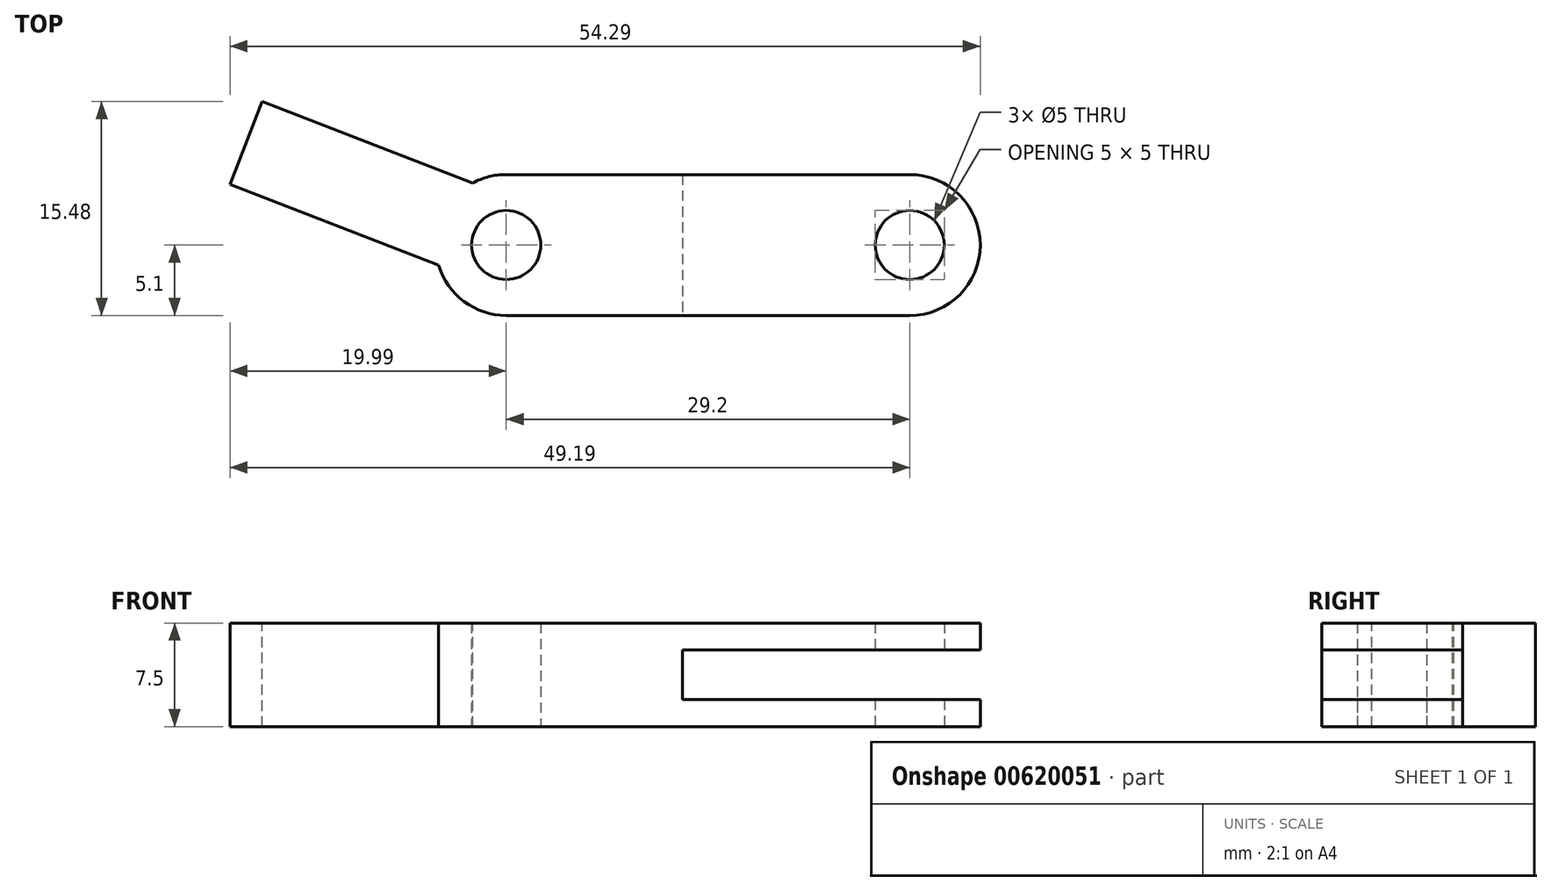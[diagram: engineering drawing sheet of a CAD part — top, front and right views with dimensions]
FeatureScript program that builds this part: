
annotation { "Feature Type Name" : "Feature", "Feature Type Description" : "" }
export const myFeature = defineFeature(function(context is Context, id is Id, definition is map)
    precondition{}
    {
        {
            var Q0;
            Q0=qCreatedBy(makeId("Top.planeOp"),FACE);
            var sketch = newSketch(context, id + "F0", { "sketchPlane" : qUnion([Q0])});
            skLineSegment(sketch, "E0.bottom", {"start": v(0, 0) * mm, "end": v(-29.2, 0) * mm});
            skLineSegment(sketch, "E0.top", {"start": v(0, 10.2) * mm, "end": v(-29.2, 10.2) * mm});
            skLineSegment(sketch, "E0.left", {"start": v(0, 0) * mm, "end": v(0, 10.2) * mm});
            skLineSegment(sketch, "E0.right", {"start": v(-29.2, 0) * mm, "end": v(-29.2, 10.2) * mm});
            skCircle(sketch, "E1", {"center": v(-29.2, 5.1) * mm, "radius": 5.1 * mm});
            skCircle(sketch, "E2", {"center": v(0, 5.1) * mm, "radius": 5.1 * mm});
            skCircle(sketch, "E3", {"center": v(-29.2, 5.1) * mm, "radius": 2.5 * mm});
            skCircle(sketch, "E4", {"center": v(0, 5.1) * mm, "radius": 2.5 * mm});
            skSolve(sketch);
        }
        {
            var Q0;
            Q0 = qSketchRegion(id + "F0", true);
            extrude(context, id + "F1", {"entities" : qUnion([Q0]), "depth" : 7.5 * mm, "offsetDistance" : 25 * mm});
        }
        {
            var Q0;
            Q0=makeQuery(id+"F1.opExtrude","SWEPT_FACE",FACE,{"disambiguationData":[OSD([sQuery(id+"F0.wireOp",EDGE,"E0.bottom")])]});
            var sketch = newSketch(context, id + "F2", { "sketchPlane" : qUnion([Q0])});
            skLineSegment(sketch, "E5.bottom", {"start": v(-16.44, 5.55) * mm, "end": v(11.99, 5.55) * mm});
            skLineSegment(sketch, "E5.top", {"start": v(-16.44, 1.95) * mm, "end": v(11.99, 1.95) * mm});
            skLineSegment(sketch, "E5.left", {"start": v(-16.44, 5.55) * mm, "end": v(-16.44, 1.95) * mm});
            skLineSegment(sketch, "E5.right", {"start": v(11.99, 5.55) * mm, "end": v(11.99, 1.95) * mm});
            skPoint(sketch, "E6", {"position": v(0, 7.5) * mm});
            skPoint(sketch, "E7", {"position": v(0, 5.55) * mm});
            skPoint(sketch, "E8", {"position": v(0, 1.95) * mm});
            skPoint(sketch, "E9", {"position": v(0, 0) * mm});
            skLineSegment(sketch, "E10", {"start": v(0, 7.5) * mm, "end": v(0, 5.55) * mm, "construction": true});
            skLineSegment(sketch, "E11", {"start": v(0, 1.95) * mm, "end": v(0, 0) * mm, "construction": true});
            skSolve(sketch);
        }
        {
            var Q0;
            Q0 = qSketchRegion(id + "F2", true);
            extrude(context, id + "F3", {"entities" : qUnion([Q0]), "operationType" : NewBodyOperationType.REMOVE, "endBound" : BoundingType.THROUGH_ALL, "oppositeDirection" : true, "depth" : 25 * mm, "offsetDistance" : 25 * mm});
        }
        {
            var Q0;
            Q0=makeQuery(id+"F1.opExtrude","CAP_FACE",FACE,{"disambiguationData":[OSD([sQuery(id+"F0.wireOp",EDGE,"E0.bottom"),sQuery(id+"F0.wireOp",EDGE,"E0.top"),sQuery(id+"F0.wireOp",EDGE,"E1"),sQuery(id+"F0.wireOp",EDGE,"E2"),sQuery(id+"F0.wireOp",EDGE,"E3"),sQuery(id+"F0.wireOp",EDGE,"E4")])],"isStart":false});
            var sketch = newSketch(context, id + "F4", { "sketchPlane" : qUnion([Q0])});
            skLineSegment(sketch, "E12", {"start": v(-30.34, 9.08) * mm, "end": v(-32.66, 3.09) * mm});
            skLineSegment(sketch, "E13", {"start": v(-32.66, 3.09) * mm, "end": v(-49.2, 9.48) * mm});
            skLineSegment(sketch, "E14", {"start": v(-49.2, 9.48) * mm, "end": v(-46.87, 15.48) * mm});
            skLineSegment(sketch, "E15", {"start": v(-46.87, 15.48) * mm, "end": v(-30.34, 9.08) * mm});
            skSolve(sketch);
        }
        {
            var Q0;
            {var subQ0=sQuery(id+"F4.wireOp",EDGE,"E14");Q0=makeQuery(id+"F4.imprint","IMPRINT",FACE,{"disambiguationData":[TD([[makeQuery(id+"F4.imprint","IMPRINT",EDGE,{"derivedFrom":subQ0}),-1.0]])]});}
            extrude(context, id + "F5", {"entities" : qUnion([Q0]), "operationType" : NewBodyOperationType.ADD, "oppositeDirection" : true, "depth" : 7.5 * mm, "offsetDistance" : 25 * mm});
        }
    });
